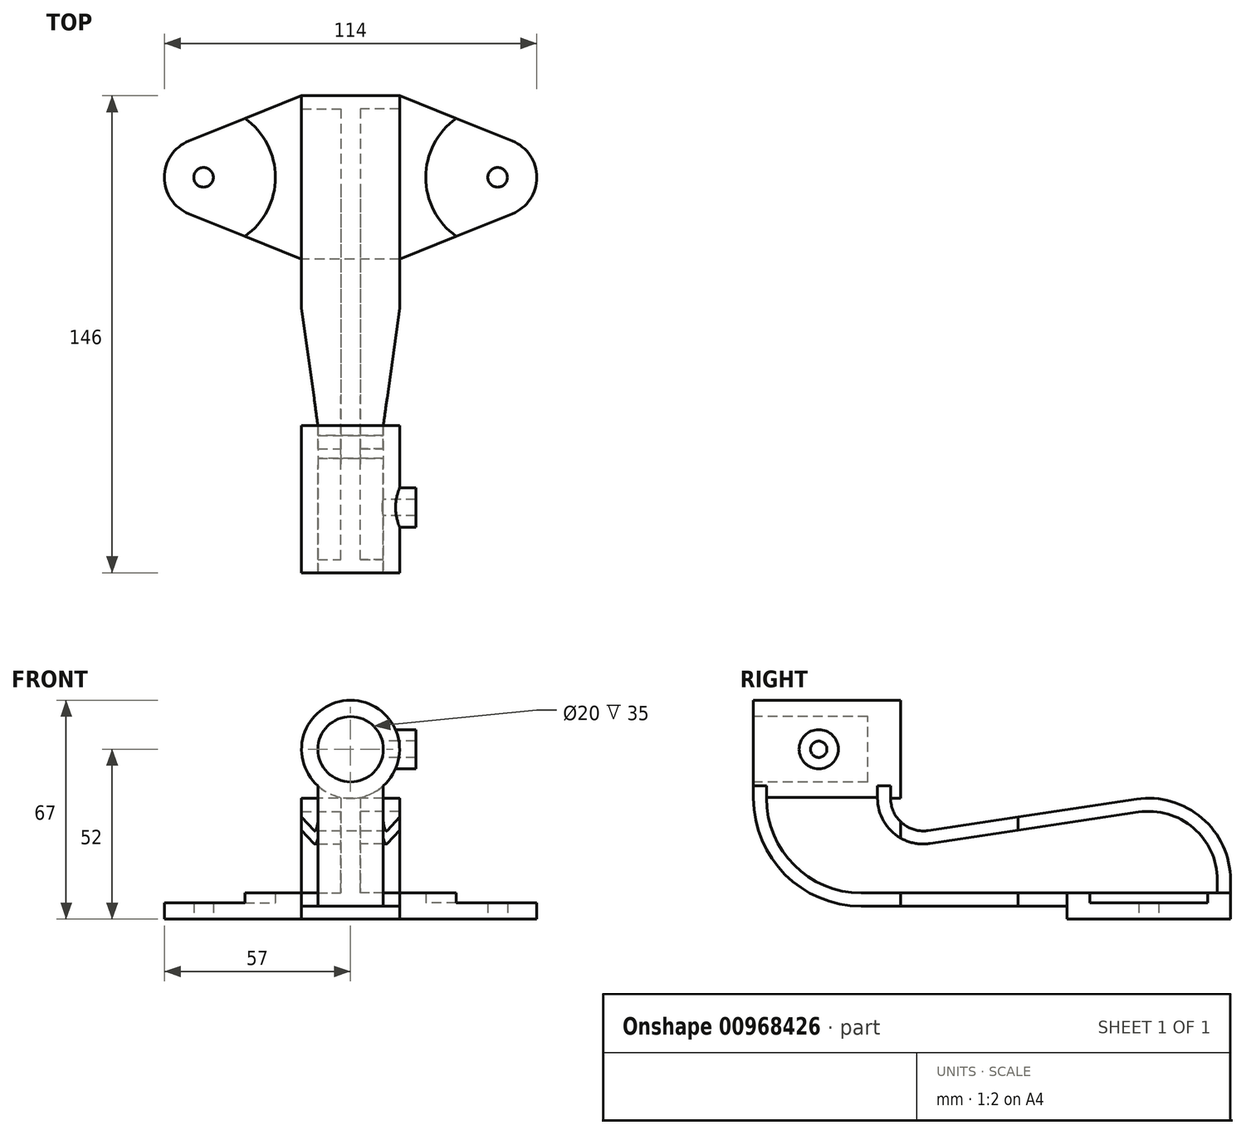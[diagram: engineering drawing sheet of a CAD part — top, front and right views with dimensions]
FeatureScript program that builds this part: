
annotation { "Feature Type Name" : "Feature", "Feature Type Description" : "" }
export const myFeature = defineFeature(function(context is Context, id is Id, definition is map)
    precondition{}
    {
        {
            var Q0;
            Q0=qCreatedBy(makeId("Top.planeOp"),FACE);
            cPlane(context, id + "F0", {"entities" : qUnion([Q0]), "cplaneType" : CPlaneType.OFFSET, "offset" : 52 * mm, "width" : 150 * mm, "height" : 150 * mm});
        }
        {
            var Q0;
            Q0=qCreatedBy(makeId("Top.planeOp"),FACE);
            var sketch = newSketch(context, id + "F1", { "sketchPlane" : qUnion([Q0])});
            skLineSegment(sketch, "E0", {"start": v(10, 0) * mm, "end": v(10, 45) * mm});
            skLineSegment(sketch, "E1", {"start": v(10, 45) * mm, "end": v(15, 81) * mm});
            skLineSegment(sketch, "E2", {"start": v(15, 81) * mm, "end": v(15, 146) * mm});
            skSolve(sketch);
        }
        {
            var Q0;
            Q0 = qConstructionFilter(qBodyType(qCreatedBy(id + "F1" ,EDGE), BodyType.WIRE), ConstructionObject.NO);
            extrude(context, id + "F2", {"bodyType" : ToolBodyType.SURFACE, "surfaceEntities" : qUnion([Q0]), "depth" : 55 * mm, "offsetDistance" : 25 * mm});
        }
        {
            var Q0;
            Q0=qCreatedBy(makeId("Right.planeOp"),FACE);
            var sketch = newSketch(context, id + "F3", { "sketchPlane" : qUnion([Q0])});
            skLineSegment(sketch, "E3", {"start": v(146, 4) * mm, "end": v(33, 4) * mm});
            skArc(sketch, "E4", {"start": v(0, 37) * mm, "mid": v(9.67, 13.67) * mm, "end": v(33, 4) * mm});
            skPoint(sketch, "E5.0", {"position": v(146, 0) * mm});
            skLineSegment(sketch, "E6", {"start": v(146, 4) * mm, "end": v(146, 0) * mm, "construction": true});
            skLineSegment(sketch, "E7.0", {"start": v(146, 8) * mm, "end": v(33, 8) * mm});
            skArc(sketch, "E7.1", {"start": v(4, 37) * mm, "mid": v(12.5, 16.5) * mm, "end": v(33, 8) * mm});
            skLineSegment(sketch, "E8", {"start": v(146, 4) * mm, "end": v(146, 8) * mm});
            skLineSegment(sketch, "E9", {"start": v(117.28, 36.72) * mm, "end": v(53.49, 27.11) * mm});
            skArc(sketch, "E10", {"start": v(42, 37) * mm, "mid": v(45.48, 29.42) * mm, "end": v(53.49, 27.11) * mm});
            skArc(sketch, "E11", {"start": v(146, 12) * mm, "mid": v(137.3, 30.95) * mm, "end": v(117.28, 36.72) * mm});
            skLineSegment(sketch, "E12", {"start": v(146, 8) * mm, "end": v(146, 12) * mm});
            skLineSegment(sketch, "E13.0", {"start": v(142, 8) * mm, "end": v(142, 12) * mm});
            skArc(sketch, "E13.1", {"start": v(142, 12) * mm, "mid": v(134.7, 27.92) * mm, "end": v(117.87, 32.77) * mm});
            skLineSegment(sketch, "E13.2", {"start": v(117.87, 32.77) * mm, "end": v(54.09, 23.16) * mm});
            skArc(sketch, "E13.3", {"start": v(38, 37) * mm, "mid": v(42.87, 26.39) * mm, "end": v(54.09, 23.16) * mm});
            skLineSegment(sketch, "E14", {"start": v(0, 37) * mm, "end": v(0, 52) * mm});
            skLineSegment(sketch, "E15", {"start": v(4, 37) * mm, "end": v(4, 52) * mm});
            skLineSegment(sketch, "E16", {"start": v(38, 37) * mm, "end": v(38, 52) * mm});
            skLineSegment(sketch, "E17", {"start": v(42, 37) * mm, "end": v(42, 52) * mm});
            skLineSegment(sketch, "E18", {"start": v(0, 52) * mm, "end": v(4, 52) * mm});
            skLineSegment(sketch, "E19", {"start": v(38, 52) * mm, "end": v(42, 52) * mm});
            skLineSegment(sketch, "E20", {"start": v(4, 52) * mm, "end": v(38, 52) * mm});
            skLineSegment(sketch, "E21", {"start": v(52, 37) * mm, "end": v(0, 37) * mm, "construction": true});
            skSolve(sketch);
        }
        {
            var Q0;
            Q0=qCreatedBy(makeId("Right.planeOp"),FACE);
            var sketch = newSketch(context, id + "F4", { "sketchPlane" : qUnion([Q0])});
            skLineSegment(sketch, "E22", {"start": v(0, 52) * mm, "end": v(0, 67) * mm});
            skLineSegment(sketch, "E23", {"start": v(0, 67) * mm, "end": v(45, 67) * mm});
            skLineSegment(sketch, "E24", {"start": v(45, 67) * mm, "end": v(45, 52) * mm});
            skLineSegment(sketch, "E25", {"start": v(45, 52) * mm, "end": v(0, 52) * mm});
            skLineSegment(sketch, "E26", {"start": v(0, 62) * mm, "end": v(35, 62) * mm});
            skLineSegment(sketch, "E27", {"start": v(35, 62) * mm, "end": v(35, 52) * mm});
            skSolve(sketch);
        }
        {
            var Q0;
            Q0=qCreatedBy(makeId("Top.planeOp"),FACE);
            var sketch = newSketch(context, id + "F5", { "sketchPlane" : qUnion([Q0])});
            skLineSegment(sketch, "E28", {"start": v(0, 146) * mm, "end": v(15, 146) * mm});
            skLineSegment(sketch, "E29", {"start": v(15, 146) * mm, "end": v(49.48, 132.13) * mm});
            skLineSegment(sketch, "E30", {"start": v(49.48, 109.87) * mm, "end": v(15, 96) * mm});
            skLineSegment(sketch, "E31", {"start": v(15, 96) * mm, "end": v(0, 96) * mm});
            skLineSegment(sketch, "E32", {"start": v(0, 96) * mm, "end": v(0, 146) * mm});
            skLineSegment(sketch, "E33", {"start": v(0, 121) * mm, "end": v(77.16, 121) * mm, "construction": true});
            skPoint(sketch, "E34.visualSharp", {"position": v(77.16, 121) * mm});
            skArc(sketch, "E34.filletArc", {"start": v(49.48, 109.87) * mm, "mid": v(57, 121) * mm, "end": v(49.48, 132.13) * mm});
            skArc(sketch, "E35", {"start": v(32.37, 139.01) * mm, "mid": v(23, 121) * mm, "end": v(32.37, 102.99) * mm});
            skCircle(sketch, "E36", {"center": v(45, 121) * mm, "radius": 3 * mm});
            skSolve(sketch);
        }
        {
            var Q0;
            Q0=qCreatedBy(makeId("Right.planeOp"),FACE);
            var sketch = newSketch(context, id + "F6", { "sketchPlane" : qUnion([Q0])});
            skCircle(sketch, "E37", {"center": v(20, 52) * mm, "radius": 6 * mm});
            skSolve(sketch);
        }
        {
            var Q0;
            {var subQ1=sQuery(id+"F5.wireOp",EDGE,"E34.filletArc");Q0=makeQuery(id+"F5.imprint","IMPRINT",FACE,{"disambiguationData":[TD([[makeQuery(id+"F5.imprint","IMPRINT",EDGE,{"derivedFrom":subQ1}),1.0]])]});}
            extrude(context, id + "F7", {"entities" : qUnion([Q0]), "depth" : 5 * mm, "offsetDistance" : 25 * mm});
        }
        {
            var Q0;
            {var subQ4=sQuery(id+"F5.wireOp",EDGE,"E28");Q0=makeQuery(id+"F5.imprint","IMPRINT",FACE,{"disambiguationData":[TD([[makeQuery(id+"F5.imprint","IMPRINT",EDGE,{"derivedFrom":subQ4}),-1.0]])]});}
            extrude(context, id + "F8", {"entities" : qUnion([Q0]), "operationType" : NewBodyOperationType.ADD, "depth" : 8 * mm, "offsetDistance" : 25 * mm});
        }
        {
            var Q0;
            Q0=makeQuery(id+"F3.imprint","IMPRINT",FACE,{"disambiguationData":[TD([[makeQuery(id+"F3.imprint","IMPRINT",EDGE,{"derivedFrom":sQuery(id+"F3.wireOp",EDGE,"E3")}),-1.0]])]});
            var Q1;
            Q1=makeQuery(id+"F3.imprint","IMPRINT",FACE,{"disambiguationData":[TD([[makeQuery(id+"F3.imprint","IMPRINT",EDGE,{"derivedFrom":sQuery(id+"F3.wireOp",EDGE,"E9")}),1.0]])]});
            var Q2;
            Q2=makeQuery(id+"F2.opExtrude","SWEPT_BODY",BODY,{"disambiguationData":[OSD([sQuery(id+"F1.wireOp",EDGE,"E2")])]});
            extrude(context, id + "F9", {"entities" : qUnion([Q0, Q1]), "operationType" : NewBodyOperationType.ADD, "endBound" : BoundingType.UP_TO_BODY, "depth" : 25 * mm, "endBoundEntityBody" : qUnion([Q2]), "offsetDistance" : 25 * mm});
        }
        {
            var Q0;
            {var subQ1=sQuery(id+"F3.wireOp",EDGE,"E7.1");Q0=makeQuery(id+"F3.imprint","IMPRINT",FACE,{"disambiguationData":[TD([[makeQuery(id+"F3.imprint","IMPRINT",EDGE,{"derivedFrom":subQ1}),1.0]])]});}
            extrude(context, id + "F10", {"entities" : qUnion([Q0]), "operationType" : NewBodyOperationType.ADD, "depth" : 3 * mm, "offsetDistance" : 25 * mm});
        }
        {
            var Q0;
            Q0=makeQuery(id+"F7.opExtrude","SWEPT_BODY",BODY,{"disambiguationData":[OSD([sQuery(id+"F5.wireOp",EDGE,"E29"),sQuery(id+"F5.wireOp",EDGE,"E30"),sQuery(id+"F5.wireOp",EDGE,"E34.filletArc"),sQuery(id+"F5.wireOp",EDGE,"E35"),sQuery(id+"F5.wireOp",EDGE,"E36")])]});
            var Q1;
            Q1=qCreatedBy(makeId("Right.planeOp"),FACE);
            mirror(context, id + "F11", {"operationType" : NewBodyOperationType.ADD, "entities" : qUnion([Q0]), "mirrorPlane" : qUnion([Q1])});
        }
        {
            var Q0;
            {var subQ3=sQuery(id+"F4.wireOp",EDGE,"E23");Q0=makeQuery(id+"F4.imprint","IMPRINT",FACE,{"disambiguationData":[TD([[makeQuery(id+"F4.imprint","IMPRINT",EDGE,{"derivedFrom":subQ3}),-1.0]])]});}
            var Q1;
            {var subQ3=sQuery(id+"F4.wireOp",EDGE,"E26");Q1=makeQuery(id+"F4.imprint","IMPRINT",FACE,{"disambiguationData":[TD([[makeQuery(id+"F4.imprint","IMPRINT",EDGE,{"derivedFrom":subQ3}),-1.0]])]});}
            var Q2;
            Q2=sQuery(id+"F4.wireOp",EDGE,"E25");
            revolve(context, id + "F12", {"operationType" : NewBodyOperationType.ADD, "surfaceOperationType" : NewSurfaceOperationType.NEW, "entities" : qUnion([Q0, Q1]), "axis" : qUnion([Q2]), "revolveType" : RevolveType.FULL});
        }
        {
            var Q0;
            Q0 = qSketchRegion(id + "F6", true);
            extrude(context, id + "F13", {"entities" : qUnion([Q0]), "operationType" : NewBodyOperationType.ADD, "depth" : 20 * mm, "offsetDistance" : 25 * mm});
        }
        {
            var Q0;
            {var subQ3=sQuery(id+"F4.wireOp",EDGE,"E26");Q0=makeQuery(id+"F4.imprint","IMPRINT",FACE,{"disambiguationData":[TD([[makeQuery(id+"F4.imprint","IMPRINT",EDGE,{"derivedFrom":subQ3}),-1.0]])]});}
            var Q1;
            Q1=sQuery(id+"F4.wireOp",EDGE,"E25");
            revolve(context, id + "F14", {"operationType" : NewBodyOperationType.REMOVE, "surfaceOperationType" : NewSurfaceOperationType.NEW, "entities" : qUnion([Q0]), "axis" : qUnion([Q1]), "revolveType" : RevolveType.FULL, "oppositeDirection" : true});
        }
        {
            var Q0;
            Q0=makeQuery(id+"F13.opExtrude","CAP_FACE",FACE,{"disambiguationData":[OSD([sQuery(id+"F6.wireOp",EDGE,"E37")])],"isStart":false});
            var sketch = newSketch(context, id + "F15", { "sketchPlane" : qUnion([Q0])});
            skPoint(sketch, "E38.0", {"position": v(20, 52) * mm});
            skSolve(sketch);
        }
        {
            var Q0;
            Q0=sQuery(id+"F15.wireOp",VERTEX,"E38.0");
            var Q1;
            Q1=makeQuery(id+"F7.opExtrude","SWEPT_BODY",BODY,{"disambiguationData":[OSD([sQuery(id+"F5.wireOp",EDGE,"E29"),sQuery(id+"F5.wireOp",EDGE,"E30"),sQuery(id+"F5.wireOp",EDGE,"E34.filletArc"),sQuery(id+"F5.wireOp",EDGE,"E35"),sQuery(id+"F5.wireOp",EDGE,"E36")])]});
            hole(context, id + "F16", {"style" : HoleStyle.SIMPLE, "endStyle" : HoleEndStyle.BLIND, "standardTappedOrClearance" : lookupTablePath({ "standard" : "ISO", "engagement" : "75%", "pitch" : "1 mm", "size" : "M6", "type" : "Tapped" }), "standardBlindInLast" : lookupTablePath({ "standard" : "ISO", "fit" : "Normal", "engagement" : "75%", "pitch" : "1 mm", "size" : "M6", "type" : "Clearance & tapped" }), "holeDiameter" : 5 * mm, "majorDiameter" : 6 * mm, "showTappedDepth" : true, "holeDepth" : 11 * mm, "isTappedThrough" : true, "tappedDepth" : 11 * mm, "tapClearance" : 0, "startFromSketch" : true, "locations" : qUnion([Q0]), "scope" : qUnion([Q1])});
        }
    });
